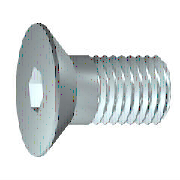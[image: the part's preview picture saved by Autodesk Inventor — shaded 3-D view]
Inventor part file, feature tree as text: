
AUTODESK INVENTOR PART (.ipt)
format: ipt  version: 2012 (Build 160160000, 160)  size: 181,248 bytes
history: native  units: mm (DEFAULTED — no unit token found)
features: extrude x1, plane x1
ambient origin geometry x7: Origin, YZ Plane, XY Plane, X Axis, Y Axis, Z Axis, Center Point
bodies: Solid1 (feature_tree), Body (feature_tree)
feature tree (2):
  extrude  "Slot"  Depth=12.7mm
  plane  "Work Plane1"
